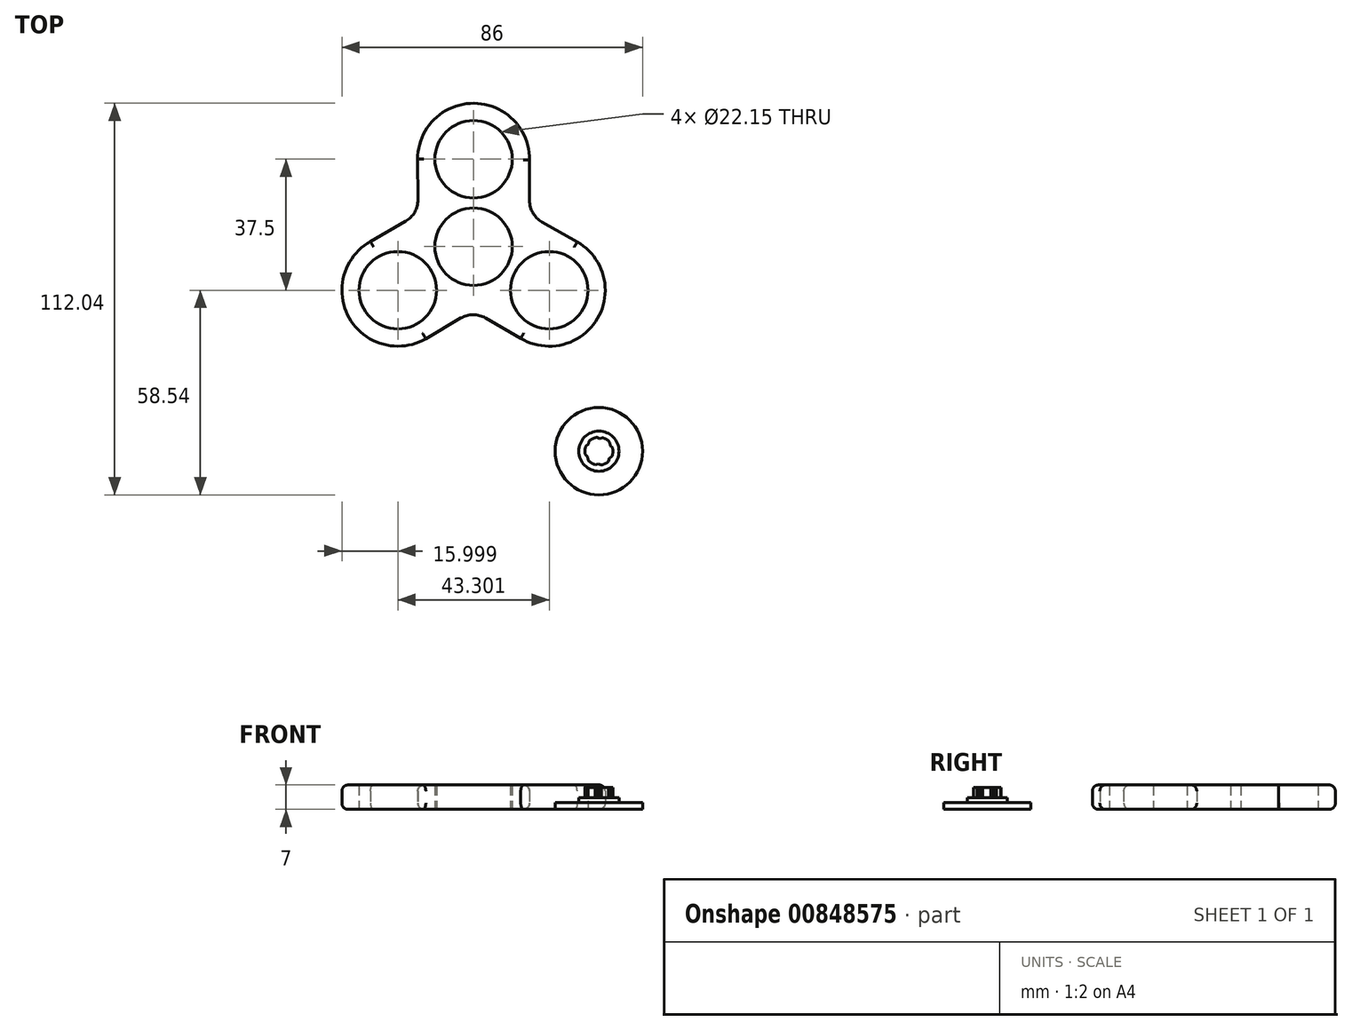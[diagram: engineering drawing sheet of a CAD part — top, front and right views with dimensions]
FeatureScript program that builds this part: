
annotation { "Feature Type Name" : "Feature", "Feature Type Description" : "" }
export const myFeature = defineFeature(function(context is Context, id is Id, definition is map)
    precondition{}
    {
        {
            var Q0;
            Q0=qCreatedBy(makeId("Top.planeOp"),FACE);
            var sketch = newSketch(context, id + "F0", { "sketchPlane" : qUnion([Q0])});
            skCircle(sketch, "E0", {"center": v(0, 0) * mm, "radius": 11.07 * mm});
            skCircle(sketch, "E1", {"center": v(0, 25) * mm, "radius": 11.07 * mm});
            skArc(sketch, "E2", {"start": v(16, 24.8) * mm, "mid": v(0.1, 41) * mm, "end": v(-16, 25) * mm});
            skLineSegment(sketch, "E3", {"start": v(-16, 0) * mm, "end": v(-16, 0) * mm});
            skLineSegment(sketch, "E4", {"start": v(16, 24.8) * mm, "end": v(16, 9.09) * mm});
            skPoint(sketch, "E5.center", {"position": v(-2.59, -4.52) * mm});
            skPoint(sketch, "E6.orphan", {"position": v(-15.8, 9.32) * mm});
            skPoint(sketch, "E7.orphan", {"position": v(0.2, -18.39) * mm});
            skPoint(sketch, "E8.orphan", {"position": v(8.03, 4.84) * mm});
            skPoint(sketch, "E9.orphan", {"position": v(16, 0) * mm});
            skLineSegment(sketch, "E10", {"start": v(-16, 25) * mm, "end": v(-15.87, 9.31) * mm});
            skArc(sketch, "E11.1.0", {"start": v(-29.48, 1.45) * mm, "mid": v(-35.55, -20.42) * mm, "end": v(-13.65, -26.36) * mm});
            skLineSegment(sketch, "E11.1.1", {"start": v(-13.65, -26.36) * mm, "end": v(-0.13, -18.4) * mm});
            skLineSegment(sketch, "E11.1.2", {"start": v(-29.48, 1.45) * mm, "end": v(-15.87, 9.31) * mm});
            skCircle(sketch, "E11.1.3", {"center": v(-21.65, -12.5) * mm, "radius": 11.07 * mm});
            skArc(sketch, "E11.2.0", {"start": v(13.48, -26.26) * mm, "mid": v(35.46, -20.58) * mm, "end": v(29.65, 1.36) * mm});
            skLineSegment(sketch, "E11.2.1", {"start": v(29.65, 1.36) * mm, "end": v(16, 9.09) * mm});
            skLineSegment(sketch, "E11.2.2", {"start": v(13.48, -26.26) * mm, "end": v(-0.13, -18.4) * mm});
            skCircle(sketch, "E11.2.3", {"center": v(21.65, -12.5) * mm, "radius": 11.07 * mm});
            skPoint(sketch, "E12.orphan", {"position": v(7.9, 13.68) * mm});
            skPoint(sketch, "E13.orphan", {"position": v(16, 0.24) * mm});
            skPoint(sketch, "E14.orphan", {"position": v(7.9, -13.68) * mm});
            skPoint(sketch, "E15.orphan", {"position": v(-7.8, -13.98) * mm});
            skPoint(sketch, "E16.orphan", {"position": v(-15.8, 0) * mm});
            skPoint(sketch, "E17.orphan", {"position": v(-8.2, 13.74) * mm});
            skSolve(sketch);
        }
        {
            var Q0;
            Q0=makeQuery(id+"F0.imprint","IMPRINT",FACE,{"disambiguationData":[TD([[makeQuery(id+"F0.imprint","IMPRINT",EDGE,{"derivedFrom":sQuery(id+"F0.wireOp",EDGE,"E0")}),-1.0]])]});
            extrude(context, id + "F1", {"entities" : qUnion([Q0]), "depth" : 7 * mm, "offsetDistance" : 25 * mm});
        }
        {
            var Q0;
            Q0=makeQuery(id+"F1.opExtrude","SWEPT_EDGE",EDGE,{"disambiguationData":[OSD([sQuery(id+"F0.wireOp",EDGE,"E4"),sQuery(id+"F0.wireOp",EDGE,"E11.2.1")])]});
            var Q1;
            Q1=makeQuery(id+"F1.opExtrude","SWEPT_EDGE",EDGE,{"disambiguationData":[OSD([sQuery(id+"F0.wireOp",EDGE,"E10"),sQuery(id+"F0.wireOp",EDGE,"E11.1.2")])]});
            var Q2;
            Q2=makeQuery(id+"F1.opExtrude","SWEPT_EDGE",EDGE,{"disambiguationData":[OSD([sQuery(id+"F0.wireOp",EDGE,"E11.1.1"),sQuery(id+"F0.wireOp",EDGE,"E11.2.2")])]});
            fillet(context, id + "F2", {"entities" : qUnion([Q0, Q1, Q2]), "radius" : 7 * mm, "tangentPropagation" : true, "allowEdgeOverflow" : false});
        }
        {
            var Q0;
            Q0=qCreatedBy(makeId("Top.planeOp"),FACE);
            var sketch = newSketch(context, id + "F3", { "sketchPlane" : qUnion([Q0])});
            skCircle(sketch, "E18", {"center": v(35.85, -58.54) * mm, "radius": 12.5 * mm});
            skSolve(sketch);
        }
        {
            var Q0;
            Q0=makeQuery(id+"F3.imprint","IMPRINT",FACE,{"disambiguationData":[TD([[makeQuery(id+"F3.imprint","IMPRINT",EDGE,{"derivedFrom":sQuery(id+"F3.wireOp",EDGE,"E18")}),1.0]])]});
            extrude(context, id + "F4", {"entities" : qUnion([Q0]), "depth" : 2 * mm, "offsetDistance" : 25 * mm});
        }
        {
            var Q0;
            Q0=makeQuery(id+"F4.opExtrude","CAP_FACE",FACE,{"disambiguationData":[OSD([sQuery(id+"F3.wireOp",EDGE,"E18")])],"isStart":false});
            var sketch = newSketch(context, id + "F5", { "sketchPlane" : qUnion([Q0])});
            skCircle(sketch, "E19", {"center": v(35.85, -58.54) * mm, "radius": 5.75 * mm});
            skSolve(sketch);
        }
        {
            var Q0;
            Q0=makeQuery(id+"F5.imprint","IMPRINT",FACE,{"disambiguationData":[TD([[makeQuery(id+"F5.imprint","IMPRINT",EDGE,{"derivedFrom":sQuery(id+"F5.wireOp",EDGE,"E19")}),1.0]])]});
            extrude(context, id + "F6", {"entities" : qUnion([Q0]), "operationType" : NewBodyOperationType.ADD, "depth" : 1.3 * mm, "offsetDistance" : 25 * mm});
        }
        {
            var Q0;
            Q0=makeQuery(id+"F6.opExtrude","CAP_FACE",FACE,{"disambiguationData":[OSD([sQuery(id+"F5.wireOp",EDGE,"E19")])],"isStart":false});
            var sketch = newSketch(context, id + "F7", { "sketchPlane" : qUnion([Q0])});
            skCircle(sketch, "E20", {"center": v(35.85, -58.54) * mm, "radius": 4 * mm});
            skSolve(sketch);
        }
        {
            var Q0;
            Q0=makeQuery(id+"F7.imprint","IMPRINT",FACE,{"disambiguationData":[TD([[makeQuery(id+"F7.imprint","IMPRINT",EDGE,{"derivedFrom":sQuery(id+"F7.wireOp",EDGE,"E20")}),1.0]])]});
            extrude(context, id + "F8", {"entities" : qUnion([Q0]), "operationType" : NewBodyOperationType.ADD, "depth" : 3 * mm, "offsetDistance" : 25 * mm});
        }
        {
            var Q0;
            Q0=makeQuery(id+"F1.opExtrude","CAP_EDGE",EDGE,{"disambiguationData":[OSD([sQuery(id+"F0.wireOp",EDGE,"E11.1.0")])],"isStart":false});
            var Q1;
            Q1=makeQuery(id+"F1.opExtrude","CAP_EDGE",EDGE,{"disambiguationData":[OSD([sQuery(id+"F0.wireOp",EDGE,"E11.1.1")])],"isStart":false});
            var Q2;
            Q2=makeQuery(id+"F1.opExtrude","CAP_EDGE",EDGE,{"disambiguationData":[OSD([sQuery(id+"F0.wireOp",EDGE,"E11.2.0")])],"isStart":false});
            var Q3;
            Q3=makeQuery(id+"F1.opExtrude","CAP_EDGE",EDGE,{"disambiguationData":[OSD([sQuery(id+"F0.wireOp",EDGE,"E11.2.1")])],"isStart":false});
            var Q4;
            Q4=makeQuery(id+"F1.opExtrude","CAP_EDGE",EDGE,{"disambiguationData":[OSD([sQuery(id+"F0.wireOp",EDGE,"E2")])],"isStart":false});
            var Q5;
            Q5=makeQuery(id+"F1.opExtrude","CAP_EDGE",EDGE,{"disambiguationData":[OSD([sQuery(id+"F0.wireOp",EDGE,"E10")])],"isStart":false});
            fillet(context, id + "F9", {"entities" : qUnion([Q0, Q1, Q2, Q3, Q4, Q5]), "radius" : 1.8 * mm, "tangentPropagation" : true, "allowEdgeOverflow" : false});
        }
        {
            var Q0;
            Q0=makeQuery(id+"F1.opExtrude","CAP_EDGE",EDGE,{"disambiguationData":[OSD([sQuery(id+"F0.wireOp",EDGE,"E11.2.0")])],"isStart":true});
            var Q1;
            Q1=makeQuery(id+"F1.opExtrude","CAP_EDGE",EDGE,{"disambiguationData":[OSD([sQuery(id+"F0.wireOp",EDGE,"E11.2.2")])],"isStart":true});
            var Q2;
            Q2=makeQuery(id+"F1.opExtrude","CAP_EDGE",EDGE,{"disambiguationData":[OSD([sQuery(id+"F0.wireOp",EDGE,"E11.1.1")])],"isStart":true});
            var Q3;
            Q3=makeQuery(id+"F1.opExtrude","CAP_EDGE",EDGE,{"disambiguationData":[OSD([sQuery(id+"F0.wireOp",EDGE,"E11.1.0")])],"isStart":true});
            var Q4;
            Q4=makeQuery(id+"F1.opExtrude","CAP_EDGE",EDGE,{"disambiguationData":[OSD([sQuery(id+"F0.wireOp",EDGE,"E11.1.2")])],"isStart":true});
            var Q5;
            Q5=makeQuery(id+"F1.opExtrude","CAP_EDGE",EDGE,{"disambiguationData":[OSD([sQuery(id+"F0.wireOp",EDGE,"E2")])],"isStart":true});
            var Q6;
            Q6=makeQuery(id+"F1.opExtrude","CAP_EDGE",EDGE,{"disambiguationData":[OSD([sQuery(id+"F0.wireOp",EDGE,"E4")])],"isStart":true});
            fillet(context, id + "F10", {"entities" : qUnion([Q0, Q1, Q2, Q3, Q4, Q5, Q6]), "radius" : 1.8 * mm, "tangentPropagation" : true, "allowEdgeOverflow" : false});
        }
        {
            var Q0;
            Q0=makeQuery(id+"F8.opExtrude","CAP_FACE",FACE,{"disambiguationData":[OSD([sQuery(id+"F7.wireOp",EDGE,"E20")])],"isStart":false});
            var sketch = newSketch(context, id + "F11", { "sketchPlane" : qUnion([Q0])});
            skCircle(sketch, "E21.0", {"center": v(35.85, -58.54) * mm, "radius": 4 * mm});
            skLineSegment(sketch, "E22", {"start": v(35.25, -54.59) * mm, "end": v(36.1, -54.91) * mm});
            skLineSegment(sketch, "E23", {"start": v(36.1, -54.91) * mm, "end": v(36.93, -54.69) * mm});
            skLineSegment(sketch, "E24.1.0", {"start": v(32.13, -57.08) * mm, "end": v(32.83, -56.52) * mm});
            skLineSegment(sketch, "E24.1.1", {"start": v(32.83, -56.52) * mm, "end": v(33.06, -55.68) * mm});
            skLineSegment(sketch, "E24.2.0", {"start": v(32.73, -61.04) * mm, "end": v(32.59, -60.15) * mm});
            skLineSegment(sketch, "E24.2.1", {"start": v(32.59, -60.15) * mm, "end": v(31.98, -59.53) * mm});
            skLineSegment(sketch, "E24.3.0", {"start": v(36.46, -62.5) * mm, "end": v(35.61, -62.17) * mm});
            skLineSegment(sketch, "E24.3.1", {"start": v(35.61, -62.17) * mm, "end": v(34.77, -62.4) * mm});
            skLineSegment(sketch, "E24.4.0", {"start": v(39.58, -60) * mm, "end": v(38.87, -60.56) * mm});
            skLineSegment(sketch, "E24.4.1", {"start": v(38.87, -60.56) * mm, "end": v(38.65, -61.4) * mm});
            skLineSegment(sketch, "E24.5.0", {"start": v(38.98, -56.04) * mm, "end": v(39.12, -56.93) * mm});
            skLineSegment(sketch, "E24.5.1", {"start": v(39.12, -56.93) * mm, "end": v(39.73, -57.55) * mm});
            skSolve(sketch);
        }
        {
            var Q0;
            {var subQ0=sQuery(id+"F11.wireOp",EDGE,"E24.5.0");Q0=makeQuery(id+"F11.imprint","IMPRINT",FACE,{"disambiguationData":[TD([[makeQuery(id+"F11.imprint","IMPRINT",EDGE,{"derivedFrom":subQ0}),1.0]])]});}
            var Q1;
            {var subQ0=sQuery(id+"F11.wireOp",EDGE,"E22");Q1=makeQuery(id+"F11.imprint","IMPRINT",FACE,{"disambiguationData":[TD([[makeQuery(id+"F11.imprint","IMPRINT",EDGE,{"derivedFrom":subQ0}),1.0]])]});}
            var Q2;
            {var subQ0=sQuery(id+"F11.wireOp",EDGE,"E24.1.0");Q2=makeQuery(id+"F11.imprint","IMPRINT",FACE,{"disambiguationData":[TD([[makeQuery(id+"F11.imprint","IMPRINT",EDGE,{"derivedFrom":subQ0}),1.0]])]});}
            var Q3;
            {var subQ0=sQuery(id+"F11.wireOp",EDGE,"E24.2.0");Q3=makeQuery(id+"F11.imprint","IMPRINT",FACE,{"disambiguationData":[TD([[makeQuery(id+"F11.imprint","IMPRINT",EDGE,{"derivedFrom":subQ0}),1.0]])]});}
            var Q4;
            {var subQ0=sQuery(id+"F11.wireOp",EDGE,"E24.3.0");Q4=makeQuery(id+"F11.imprint","IMPRINT",FACE,{"disambiguationData":[TD([[makeQuery(id+"F11.imprint","IMPRINT",EDGE,{"derivedFrom":subQ0}),1.0]])]});}
            var Q5;
            {var subQ0=sQuery(id+"F11.wireOp",EDGE,"E24.4.0");Q5=makeQuery(id+"F11.imprint","IMPRINT",FACE,{"disambiguationData":[TD([[makeQuery(id+"F11.imprint","IMPRINT",EDGE,{"derivedFrom":subQ0}),1.0]])]});}
            var Q6;
            Q6=makeQuery(id+"F6.opExtrude","CAP_FACE",FACE,{"disambiguationData":[OSD([sQuery(id+"F5.wireOp",EDGE,"E19")])],"isStart":false});
            extrude(context, id + "F12", {"entities" : qUnion([Q0, Q1, Q2, Q3, Q4, Q5]), "operationType" : NewBodyOperationType.REMOVE, "endBound" : BoundingType.UP_TO_SURFACE, "oppositeDirection" : true, "depth" : 25 * mm, "endBoundEntityFace" : qUnion([Q6]), "offsetDistance" : 25 * mm});
        }
    });
